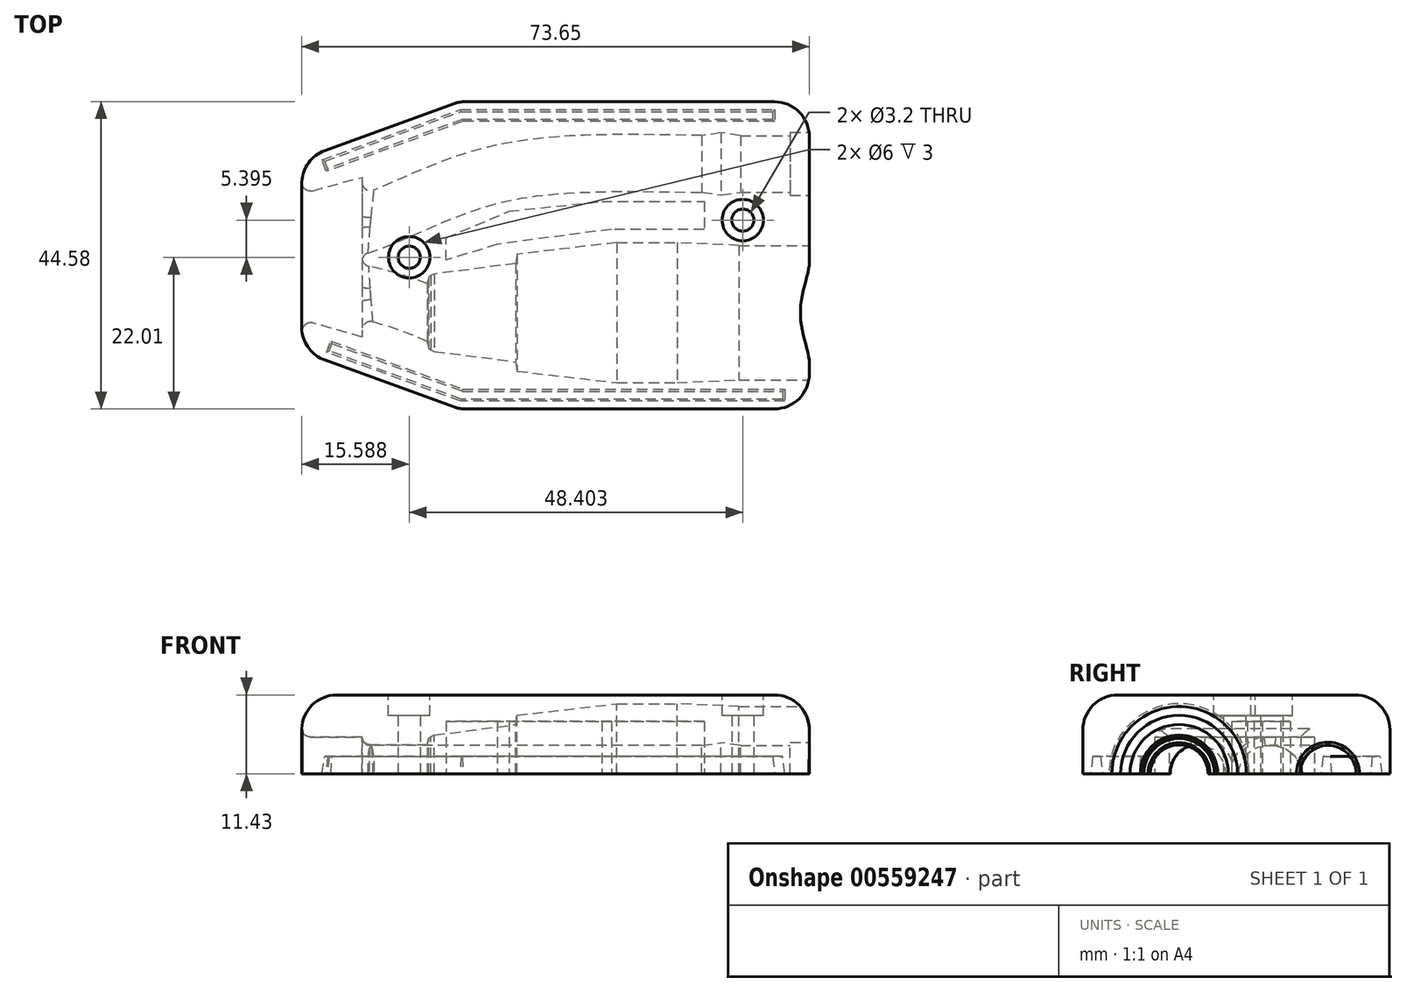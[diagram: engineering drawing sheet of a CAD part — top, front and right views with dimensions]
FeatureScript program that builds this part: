
annotation { "Feature Type Name" : "Feature", "Feature Type Description" : "" }
export const myFeature = defineFeature(function(context is Context, id is Id, definition is map)
    precondition{}
    {
        {
            var Q0;
            Q0=qCreatedBy(makeId("Top.planeOp"),FACE);
            var sketch = newSketch(context, id + "F0", { "sketchPlane" : qUnion([Q0])});
            skLineSegment(sketch, "E0", {"start": v(-29.16, 2.44) * mm, "end": v(45.25, 2.44) * mm});
            skLineSegment(sketch, "E1", {"start": v(45.25, 2.44) * mm, "end": v(45.25, -7.31) * mm});
            skLineSegment(sketch, "E2", {"start": v(45.25, -7.31) * mm, "end": v(33.01, -7.3) * mm});
            skLineSegment(sketch, "E3", {"start": v(33.01, -7.3) * mm, "end": v(31, -7.31) * mm});
            skLineSegment(sketch, "E4", {"start": v(31, -7.31) * mm, "end": v(16, -7.31) * mm});
            skLineSegment(sketch, "E5", {"start": v(16, -7.31) * mm, "end": v(7, -7.72) * mm});
            skLineSegment(sketch, "E6", {"start": v(7, -7.72) * mm, "end": v(-1.71, -7.72) * mm});
            skLineSegment(sketch, "E7", {"start": v(-1.71, -7.72) * mm, "end": v(-16.21, -6.04) * mm});
            skLineSegment(sketch, "E8", {"start": v(-16.21, -6.04) * mm, "end": v(-16.37, -4.7) * mm});
            skLineSegment(sketch, "E9", {"start": v(-16.37, -4.7) * mm, "end": v(-28.19, -3.17) * mm});
            skLineSegment(sketch, "E10", {"start": v(-28.19, -3.17) * mm, "end": v(-28.73, -2.96) * mm});
            skLineSegment(sketch, "E11", {"start": v(-28.73, -2.96) * mm, "end": v(-29.03, -2.68) * mm});
            skLineSegment(sketch, "E12", {"start": v(-29.03, -2.68) * mm, "end": v(-29.18, -2.06) * mm});
            skLineSegment(sketch, "E13", {"start": v(-29.18, -2.06) * mm, "end": v(-29.16, 2.44) * mm});
            skLineSegment(sketch, "E14.top", {"start": v(29.2, 18.83) * mm, "end": v(41.5, 18.83) * mm});
            skLineSegment(sketch, "E14.right", {"start": v(41.5, 24.03) * mm, "end": v(41.5, 18.83) * mm});
            skLineSegment(sketch, "E15", {"start": v(29.2, 19.46) * mm, "end": v(23.4, 19.46) * mm});
            skLineSegment(sketch, "E16", {"start": v(23.4, 19.46) * mm, "end": v(23.4, 24.03) * mm});
            skLineSegment(sketch, "E17", {"start": v(41.5, 24.03) * mm, "end": v(23.4, 24.03) * mm});
            skLineSegment(sketch, "E18", {"start": v(29.2, 18.83) * mm, "end": v(29.2, 19.46) * mm});
            skLineSegment(sketch, "E19.MirrorCS", {"start": v(-28.73, 7.85) * mm, "end": v(-29.03, 7.56) * mm});
            skLineSegment(sketch, "E20.MirrorCS", {"start": v(-29.03, 7.56) * mm, "end": v(-29.18, 6.94) * mm});
            skLineSegment(sketch, "E21.MirrorCS", {"start": v(33.01, 12.2) * mm, "end": v(31, 12.2) * mm});
            skLineSegment(sketch, "E22.MirrorCS", {"start": v(-28.19, 8.06) * mm, "end": v(-28.73, 7.85) * mm});
            skLineSegment(sketch, "E23.MirrorCS", {"start": v(-16.21, 10.93) * mm, "end": v(-16.37, 9.58) * mm});
            skLineSegment(sketch, "E24.MirrorCS", {"start": v(-16.37, 9.58) * mm, "end": v(-28.19, 8.06) * mm});
            skLineSegment(sketch, "E25.MirrorCS", {"start": v(7, 12.6) * mm, "end": v(-1.71, 12.6) * mm});
            skLineSegment(sketch, "E26.MirrorCS", {"start": v(45.25, 12.2) * mm, "end": v(33.01, 12.2) * mm});
            skLineSegment(sketch, "E27.MirrorCS", {"start": v(-1.71, 12.6) * mm, "end": v(-16.21, 10.93) * mm});
            skLineSegment(sketch, "E28.MirrorCS", {"start": v(16, 12.2) * mm, "end": v(7, 12.6) * mm});
            skLineSegment(sketch, "E29.MirrorCS", {"start": v(31, 12.2) * mm, "end": v(16, 12.2) * mm});
            skLineSegment(sketch, "E30.MirrorCS", {"start": v(45.25, 2.44) * mm, "end": v(45.25, 12.2) * mm});
            skLineSegment(sketch, "E31.MirrorCS", {"start": v(-29.18, 6.94) * mm, "end": v(-29.16, 2.44) * mm});
            skLineSegment(sketch, "E32", {"start": v(41.5, 20.03) * mm, "end": v(44.1, 20.03) * mm});
            skLineSegment(sketch, "E33", {"start": v(44.1, 20.03) * mm, "end": v(44.1, 24.03) * mm});
            skLineSegment(sketch, "E34", {"start": v(44.1, 24.03) * mm, "end": v(41.5, 24.03) * mm});
            skLineSegment(sketch, "E35", {"start": v(44.1, 20.03) * mm, "end": v(44.1, 19.46) * mm});
            skLineSegment(sketch, "E36", {"start": v(44.1, 19.46) * mm, "end": v(45.25, 19.46) * mm});
            skLineSegment(sketch, "E37", {"start": v(45.25, 19.46) * mm, "end": v(45.32, 24.03) * mm});
            skLineSegment(sketch, "E38", {"start": v(45.32, 24.03) * mm, "end": v(44.1, 24.03) * mm});
            skLineSegment(sketch, "E39", {"start": v(23.4, 24.03) * mm, "end": v(16.2, 24.03) * mm});
            skLineSegment(sketch, "E40", {"start": v(16.2, 24.03) * mm, "end": v(16.2, 19.93) * mm});
            skLineSegment(sketch, "E41", {"start": v(16.2, 19.93) * mm, "end": v(23.4, 19.93) * mm});
            skLineSegment(sketch, "E42", {"start": v(16.2, 19.93) * mm, "end": v(13.4, 19.53) * mm});
            skLineSegment(sketch, "E43", {"start": v(13.4, 19.53) * mm, "end": v(10.6, 19.93) * mm});
            skLineSegment(sketch, "E44", {"start": v(10.6, 19.93) * mm, "end": v(10.6, 24.03) * mm});
            skLineSegment(sketch, "E45", {"start": v(10.6, 24.03) * mm, "end": v(16.2, 24.03) * mm});
            skLineSegment(sketch, "E46.MirrorCS", {"start": v(44.1, 28.03) * mm, "end": v(44.1, 28.6) * mm});
            skLineSegment(sketch, "E47.MirrorCS", {"start": v(44.1, 28.6) * mm, "end": v(45.25, 28.6) * mm});
            skLineSegment(sketch, "E48.MirrorCS", {"start": v(29.2, 29.24) * mm, "end": v(29.2, 28.6) * mm});
            skLineSegment(sketch, "E49.MirrorCS", {"start": v(44.1, 28.03) * mm, "end": v(44.1, 24.03) * mm});
            skLineSegment(sketch, "E50.MirrorCS", {"start": v(16.2, 24.03) * mm, "end": v(16.2, 28.13) * mm});
            skLineSegment(sketch, "E51.MirrorCS", {"start": v(23.4, 28.6) * mm, "end": v(23.4, 24.03) * mm});
            skLineSegment(sketch, "E52.MirrorCS", {"start": v(10.6, 28.13) * mm, "end": v(10.6, 24.03) * mm});
            skLineSegment(sketch, "E53.MirrorCS", {"start": v(29.2, 28.6) * mm, "end": v(23.4, 28.6) * mm});
            skLineSegment(sketch, "E54.MirrorCS", {"start": v(41.5, 24.03) * mm, "end": v(41.5, 29.24) * mm});
            skLineSegment(sketch, "E55.MirrorCS", {"start": v(29.2, 29.24) * mm, "end": v(41.5, 29.24) * mm});
            skLineSegment(sketch, "E56.MirrorCS", {"start": v(45.25, 28.6) * mm, "end": v(45.32, 24.03) * mm});
            skLineSegment(sketch, "E57.MirrorCS", {"start": v(13.4, 28.53) * mm, "end": v(10.6, 28.13) * mm});
            skLineSegment(sketch, "E58.MirrorCS", {"start": v(41.5, 28.03) * mm, "end": v(44.1, 28.03) * mm});
            skLineSegment(sketch, "E59.MirrorCS", {"start": v(16.2, 28.13) * mm, "end": v(13.4, 28.53) * mm});
            skLineSegment(sketch, "E60.MirrorCS", {"start": v(16.2, 28.13) * mm, "end": v(23.4, 28.13) * mm});
            skSolve(sketch);
        }
        {
            var Q0;
            Q0=qCreatedBy(makeId("Top.planeOp"),FACE);
            var sketch = newSketch(context, id + "F1", { "sketchPlane" : qUnion([Q0])});
            skLineSegment(sketch, "E61.0", {"start": v(45.25, 2.44) * mm, "end": v(45.25, -7.31) * mm});
            skLineSegment(sketch, "E62", {"start": v(26.2, 33.05) * mm, "end": v(26.2, -11.53) * mm});
            skLineSegment(sketch, "E63", {"start": v(26.2, -11.53) * mm, "end": v(-24.6, -11.53) * mm});
            skLineSegment(sketch, "E64", {"start": v(-24.6, -11.53) * mm, "end": v(-47.46, -3.2) * mm});
            skLineSegment(sketch, "E65", {"start": v(-47.46, -3.2) * mm, "end": v(-47.46, 24.73) * mm});
            skLineSegment(sketch, "E66", {"start": v(-47.46, 24.73) * mm, "end": v(-24.6, 33.05) * mm});
            skLineSegment(sketch, "E67", {"start": v(-24.6, 33.05) * mm, "end": v(26.2, 33.05) * mm});
            skLineSegment(sketch, "E68.0", {"start": v(29.2, 29.24) * mm, "end": v(41.5, 29.24) * mm});
            skSolve(sketch);
        }
        {
            var Q0;
            Q0=qSketchRegion(id+"F1",true);
            extrude(context, id + "F2", {"entities" : qUnion([Q0]), "oppositeDirection" : true, "depth" : 0 * mm, "offsetDistance" : 25.4 * mm, "hasSecondDirection" : true, "secondDirectionOppositeDirection" : false, "secondDirectionDepth" : 11.43 * mm});
        }
        {
            var Q0;
            Q0=makeQuery(id+"F0.imprint","IMPRINT",FACE,{"disambiguationData":[TD([[makeQuery(id+"F0.imprint","IMPRINT",EDGE,{"derivedFrom":sQuery(id+"F0.wireOp",EDGE,"E0")}),-1.0]])]});
            var Q1;
            Q1=sQuery(id+"F0.wireOp",EDGE,"E0");
            revolve(context, id + "F3", {"operationType" : NewBodyOperationType.REMOVE, "entities" : qUnion([Q0]), "axis" : qUnion([Q1]), "revolveType" : RevolveType.FULL, "oppositeDirection" : true});
        }
        {
            var Q0;
            Q0=makeQuery(id+"F0.imprint","IMPRINT",FACE,{"disambiguationData":[TD([[makeQuery(id+"F0.imprint","IMPRINT",EDGE,{"derivedFrom":sQuery(id+"F0.wireOp",EDGE,"E14.top")}),1.0]])]});
            var Q1;
            Q1=makeQuery(id+"F0.imprint","IMPRINT",FACE,{"disambiguationData":[TD([[makeQuery(id+"F0.imprint","IMPRINT",EDGE,{"derivedFrom":sQuery(id+"F0.wireOp",EDGE,"E40")}),1.0]])]});
            var Q2;
            Q2=makeQuery(id+"F0.imprint","IMPRINT",FACE,{"disambiguationData":[TD([[makeQuery(id+"F0.imprint","IMPRINT",EDGE,{"derivedFrom":sQuery(id+"F0.wireOp",EDGE,"E40")}),-1.0]])]});
            var Q3;
            Q3=sQuery(id+"F0.wireOp",EDGE,"E17");
            revolve(context, id + "F4", {"operationType" : NewBodyOperationType.REMOVE, "entities" : qUnion([Q0, Q1, Q2]), "axis" : qUnion([Q3]), "revolveType" : RevolveType.FULL});
        }
        {
            var Q0;
            Q0=makeQuery(id+"F2.opExtrude","CAP_FACE",FACE,{"disambiguationData":[OSD([sQuery(id+"F1.wireOp",EDGE,"FN9DgEXL-DUnT-EqR8-ggIH-wTex11pTKOJ6"),sQuery(id+"F1.wireOp",EDGE,"Mmaicck8-LA38-ALDy-QV3c-pMFCgAv4KP83"),sQuery(id+"F1.wireOp",EDGE,"E62"),sQuery(id+"F1.wireOp",EDGE,"E63"),sQuery(id+"F1.wireOp",EDGE,"E64"),sQuery(id+"F1.wireOp",EDGE,"E65"),sQuery(id+"F1.wireOp",EDGE,"E66"),sQuery(id+"F1.wireOp",EDGE,"E67")])],"isStart":true});
            var sketch = newSketch(context, id + "F5", { "sketchPlane" : qUnion([Q0])});
            skLineSegment(sketch, "E69.0", {"start": v(-29.16, 2.44) * mm, "end": v(45.25, 2.44) * mm});
            skFitSpline(sketch, "E70", {"points": [v(-29.16, 2.44) * mm, v(-47.46, 6.7) * mm, v(-83.77, 9.93) * mm], "startDerivative": vector(-48.46, 20.5) * mm, "endDerivative": vector(-77.25, 2.74) * mm});
            skSolve(sketch);
        }
        {
            var Q0;
            Q0=sQuery(id+"F5.wireOp",VERTEX,"E70.0.internal");
            var Q1;
            Q1=sQuery(id+"F5.wireOp",EDGE,"E69.0");
            cPlane(context, id + "F6", {"entities" : qUnion([Q0, Q1]), "cplaneType" : CPlaneType.LINE_POINT, "offset" : 25.4 * mm, "width" : 152.4 * mm, "height" : 152.4 * mm});
        }
        {
            var Q0;
            Q0=qCreatedBy(id+"F6.planeOp",FACE);
            var sketch = newSketch(context, id + "F7", { "sketchPlane" : qUnion([Q0])});
            skCircle(sketch, "E71", {"center": v(2.44, 0) * mm, "radius": 4.2 * mm});
            skSolve(sketch);
        }
        {
            var Q0;
            Q0=qSketchRegion(id+"F7",true);
            var Q1;
            Q1=sQuery(id+"F5.wireOp",EDGE,"E70");
            sweep(context, id + "F8", {"operationType" : NewBodyOperationType.REMOVE, "profiles" : qUnion([Q0]), "path" : qUnion([Q1])});
        }
        {
            var Q0;
            Q0=sQuery(id+"F0.wireOp",VERTEX,"E45.start");
            var Q1;
            Q1=sQuery(id+"F0.wireOp",EDGE,"E45");
            cPlane(context, id + "F9", {"entities" : qUnion([Q0, Q1]), "cplaneType" : CPlaneType.LINE_POINT, "offset" : 25.4 * mm, "width" : 152.4 * mm, "height" : 152.4 * mm});
        }
        {
            var Q0;
            {var subQ0=sQuery(id+"F1.wireOp",EDGE,"E62");var subQ1=sQuery(id+"F1.wireOp",EDGE,"E65");var subQ2=sQuery(id+"F1.wireOp",EDGE,"E66");var subQ3=sQuery(id+"F1.wireOp",EDGE,"E67");Q0=makeQuery(id+"F8.boolean.opBoolean","SPLIT",FACE,{"disambiguationData":[TD([makeQuery(id+"F2.opExtrude","SWEPT_FACE",FACE,{"disambiguationData":[OSD([subQ2])]})])],"derivedFrom":makeQuery(id+"F2.opExtrude","CAP_FACE",FACE,{"disambiguationData":[OSD([subQ0,sQuery(id+"F1.wireOp",EDGE,"E63"),sQuery(id+"F1.wireOp",EDGE,"E64"),subQ1,subQ2,subQ3])],"isStart":true})});}
            var sketch = newSketch(context, id + "F10", { "sketchPlane" : qUnion([Q0])});
            skLineSegment(sketch, "E72.0", {"start": v(10.6, 24.03) * mm, "end": v(16.2, 24.03) * mm});
            skFitSpline(sketch, "E73", {"points": [v(10.6, 24.03) * mm, v(-17.54, 22.88) * mm, v(-35.92, 16.19) * mm, v(-61.27, 13.83) * mm], "startDerivative": vector(-66.57, 0.28) * mm, "endDerivative": vector(-121.3, 10.88) * mm});
            skSolve(sketch);
        }
        {
            var Q0;
            Q0=qCreatedBy(id+"F9.planeOp",FACE);
            var sketch = newSketch(context, id + "F11", { "sketchPlane" : qUnion([Q0])});
            skCircle(sketch, "E74", {"center": v(24.03, 0) * mm, "radius": 4.12 * mm});
            skSolve(sketch);
        }
        {
            var Q0;
            Q0=qSketchRegion(id+"F11",true);
            var Q1;
            Q1=sQuery(id+"F10.wireOp",EDGE,"E73");
            sweep(context, id + "F12", {"operationType" : NewBodyOperationType.REMOVE, "profiles" : qUnion([Q0]), "path" : qUnion([Q1])});
        }
        {
            var Q0;
            Q0=qCreatedBy(makeId("Top.planeOp"),FACE);
            var sketch = newSketch(context, id + "F13", { "sketchPlane" : qUnion([Q0])});
            skLineSegment(sketch, "E75.0", {"start": v(-24.4, 31.92) * mm, "end": v(21.2, 31.92) * mm});
            skLineSegment(sketch, "E75.1", {"start": v(-44.5, 24.6) * mm, "end": v(-24.4, 31.92) * mm});
            skPoint(sketch, "E76", {"position": v(21.2, 31.92) * mm});
            skPoint(sketch, "E77", {"position": v(-44.5, 24.6) * mm});
            skLineSegment(sketch, "E78.0", {"start": v(-24.09, 30.17) * mm, "end": v(21.2, 30.17) * mm});
            skLineSegment(sketch, "E78.1", {"start": v(-43.91, 22.96) * mm, "end": v(-24.09, 30.17) * mm});
            skLineSegment(sketch, "E79", {"start": v(21.2, 30.17) * mm, "end": v(21.2, 31.92) * mm});
            skLineSegment(sketch, "E80", {"start": v(-44.5, 24.6) * mm, "end": v(-43.91, 22.96) * mm});
            skLineSegment(sketch, "E81.0", {"start": v(-24.4, -10.4) * mm, "end": v(-43.83, -3.33) * mm});
            skLineSegment(sketch, "E81.1", {"start": v(22.64, -10.4) * mm, "end": v(-24.4, -10.4) * mm});
            skPoint(sketch, "E82", {"position": v(22.64, -10.4) * mm});
            skPoint(sketch, "E83", {"position": v(-43.83, -3.33) * mm});
            skLineSegment(sketch, "E84.0", {"start": v(-24.09, -8.65) * mm, "end": v(-43.24, -1.68) * mm});
            skLineSegment(sketch, "E84.1", {"start": v(22.64, -8.65) * mm, "end": v(-24.09, -8.65) * mm});
            skLineSegment(sketch, "E85", {"start": v(22.64, -10.4) * mm, "end": v(22.64, -8.65) * mm});
            skLineSegment(sketch, "E86", {"start": v(-43.83, -3.33) * mm, "end": v(-43.24, -1.68) * mm});
            skSolve(sketch);
        }
        {
            var Q0;
            Q0=qCreatedBy(makeId("Top.planeOp"),FACE);
            var sketch = newSketch(context, id + "F14", { "sketchPlane" : qUnion([Q0])});
            skLineSegment(sketch, "E87", {"start": v(-48.77, 19.31) * mm, "end": v(-38.71, 22.1) * mm});
            skLineSegment(sketch, "E88", {"start": v(-38.71, 22.1) * mm, "end": v(-38.71, -1.1) * mm});
            skLineSegment(sketch, "E89", {"start": v(-38.71, -1.1) * mm, "end": v(-48.92, 1.83) * mm});
            skLineSegment(sketch, "E90", {"start": v(-48.92, 1.83) * mm, "end": v(-48.77, 19.31) * mm});
            skSolve(sketch);
        }
        {
            var Q0;
            Q0=qCreatedBy(makeId("Top.planeOp"),FACE);
            var sketch = newSketch(context, id + "F15", { "sketchPlane" : qUnion([Q0])});
            skCircle(sketch, "E91", {"center": v(-31.86, 10.48) * mm, "radius": 1.6 * mm});
            skCircle(sketch, "E92", {"center": v(16.54, 15.88) * mm, "radius": 1.6 * mm});
            skSolve(sketch);
        }
        {
            var Q0;
            Q0 = qSketchRegion(id + "F13", true);
            extrude(context, id + "F16", {"entities" : qUnion([Q0]), "operationType" : NewBodyOperationType.REMOVE, "depth" : 2.5 * mm, "offsetDistance" : 25.4 * mm, "hasDraft" : true, "draftAngle" : 7 * degree, "draftPullDirection" : true});
        }
        {
            var Q0;
            Q0 = qSketchRegion(id + "F15", true);
            extrude(context, id + "F17", {"entities" : qUnion([Q0]), "operationType" : NewBodyOperationType.REMOVE, "depth" : 25.4 * mm, "offsetDistance" : 25.4 * mm});
        }
        {
            var Q0;
            Q0 = qSketchRegion(id + "F14", true);
            extrude(context, id + "F18", {"entities" : qUnion([Q0]), "operationType" : NewBodyOperationType.REMOVE, "depth" : 5.33 * mm, "offsetDistance" : 25.4 * mm});
        }
        {
            var Q0;
            Q0=makeQuery(id+"F2.opExtrude","CAP_FACE",FACE,{"disambiguationData":[OSD([sQuery(id+"F1.wireOp",EDGE,"E62"),sQuery(id+"F1.wireOp",EDGE,"E63"),sQuery(id+"F1.wireOp",EDGE,"E64"),sQuery(id+"F1.wireOp",EDGE,"E65"),sQuery(id+"F1.wireOp",EDGE,"E66"),sQuery(id+"F1.wireOp",EDGE,"E67")])],"isStart":true});
            var sketch = newSketch(context, id + "F19", { "sketchPlane" : qUnion([Q0])});
            skCircle(sketch, "E93.0", {"center": v(-31.86, 10.48) * mm, "radius": 1.6 * mm});
            skCircle(sketch, "E94.0", {"center": v(16.54, 15.88) * mm, "radius": 1.6 * mm});
            skCircle(sketch, "E95", {"center": v(-31.86, 10.48) * mm, "radius": 3 * mm});
            skCircle(sketch, "E96", {"center": v(16.54, 15.88) * mm, "radius": 3 * mm});
            skSolve(sketch);
        }
        {
            var Q0;
            Q0 = qSketchRegion(id + "F19", true);
            extrude(context, id + "F20", {"entities" : qUnion([Q0]), "operationType" : NewBodyOperationType.REMOVE, "oppositeDirection" : true, "depth" : 3 * mm, "offsetDistance" : 25.4 * mm});
        }
        {
            var Q0;
            {var subQ4=sQuery(id+"F1.wireOp",EDGE,"E62");var subQ8=makeQuery(id+"F3.boolean.opBoolean","COPY",FACE,{"derivedFrom":makeQuery(id+"F3.opRevolve","SWEPT_FACE",FACE,{"disambiguationData":[OSD([sQuery(id+"F0.wireOp",EDGE,"E4")])]})});var subQ19=sQuery(id+"F1.wireOp",EDGE,"E65");var subQ20=sQuery(id+"F1.wireOp",EDGE,"E66");var subQ21=sQuery(id+"F1.wireOp",EDGE,"E67");Q0=makeQuery(id+"F12.boolean.opBoolean","SPLIT",FACE,{"disambiguationData":[TD([subQ8])],"derivedFrom":makeQuery(id+"F8.boolean.opBoolean","SPLIT",FACE,{"disambiguationData":[TD([makeQuery(id+"F2.opExtrude","SWEPT_FACE",FACE,{"disambiguationData":[OSD([subQ20])]})])],"derivedFrom":makeQuery(id+"F2.opExtrude","CAP_FACE",FACE,{"disambiguationData":[OSD([subQ4,sQuery(id+"F1.wireOp",EDGE,"E63"),sQuery(id+"F1.wireOp",EDGE,"E64"),subQ19,subQ20,subQ21])],"isStart":false})})});}
            var sketch = newSketch(context, id + "F21", { "sketchPlane" : qUnion([Q0])});
            skLineSegment(sketch, "E97", {"start": v(-26.5, -13.3) * mm, "end": v(-17.37, -17.17) * mm});
            skLineSegment(sketch, "E98", {"start": v(-17.37, -17.17) * mm, "end": v(-3.92, -18.56) * mm});
            skLineSegment(sketch, "E99", {"start": v(-3.92, -18.56) * mm, "end": v(10.93, -18.56) * mm});
            skLineSegment(sketch, "E100", {"start": v(10.93, -18.56) * mm, "end": v(10.93, -14.54) * mm});
            skLineSegment(sketch, "E101", {"start": v(10.93, -14.54) * mm, "end": v(-2.52, -14.54) * mm});
            skLineSegment(sketch, "E102", {"start": v(-2.52, -14.54) * mm, "end": v(-19.07, -12.37) * mm});
            skLineSegment(sketch, "E103", {"start": v(-19.07, -12.37) * mm, "end": v(-26.5, -10.05) * mm});
            skLineSegment(sketch, "E104", {"start": v(-26.5, -10.05) * mm, "end": v(-26.5, -13.3) * mm});
            skSolve(sketch);
        }
        {
            var Q0;
            Q0 = qSketchRegion(id + "F21", true);
            extrude(context, id + "F22", {"entities" : qUnion([Q0]), "operationType" : NewBodyOperationType.REMOVE, "oppositeDirection" : true, "depth" : 7.62 * mm, "offsetDistance" : 25.4 * mm});
        }
        {
            var Q0;
            Q0=makeQuery(id+"F2.opExtrude","CAP_EDGE",EDGE,{"disambiguationData":[OSD([sQuery(id+"F1.wireOp",EDGE,"E65")])],"isStart":true});
            var Q1;
            Q1=makeQuery(id+"F2.opExtrude","SWEPT_EDGE",EDGE,{"disambiguationData":[OSD([sQuery(id+"F1.wireOp",EDGE,"E64"),sQuery(id+"F1.wireOp",EDGE,"E65")])]});
            var Q2;
            Q2=makeQuery(id+"F2.opExtrude","CAP_EDGE",EDGE,{"disambiguationData":[OSD([sQuery(id+"F1.wireOp",EDGE,"E64")])],"isStart":true});
            var Q3;
            Q3=makeQuery(id+"F2.opExtrude","SWEPT_EDGE",EDGE,{"disambiguationData":[OSD([sQuery(id+"F1.wireOp",EDGE,"E63"),sQuery(id+"F1.wireOp",EDGE,"E64")])]});
            var Q4;
            Q4=makeQuery(id+"F2.opExtrude","CAP_EDGE",EDGE,{"disambiguationData":[OSD([sQuery(id+"F1.wireOp",EDGE,"E63")])],"isStart":true});
            var Q5;
            Q5=makeQuery(id+"F2.opExtrude","SWEPT_EDGE",EDGE,{"disambiguationData":[OSD([sQuery(id+"F1.wireOp",EDGE,"E62"),sQuery(id+"F1.wireOp",EDGE,"E63")])]});
            var Q6;
            Q6=makeQuery(id+"F2.opExtrude","CAP_EDGE",EDGE,{"disambiguationData":[OSD([sQuery(id+"F1.wireOp",EDGE,"E62")])],"isStart":true});
            var Q7;
            Q7=makeQuery(id+"F2.opExtrude","SWEPT_EDGE",EDGE,{"disambiguationData":[OSD([sQuery(id+"F1.wireOp",EDGE,"E62"),sQuery(id+"F1.wireOp",EDGE,"E67")])]});
            var Q8;
            Q8=makeQuery(id+"F2.opExtrude","CAP_EDGE",EDGE,{"disambiguationData":[OSD([sQuery(id+"F1.wireOp",EDGE,"E67")])],"isStart":true});
            var Q9;
            Q9=makeQuery(id+"F2.opExtrude","SWEPT_EDGE",EDGE,{"disambiguationData":[OSD([sQuery(id+"F1.wireOp",EDGE,"E66"),sQuery(id+"F1.wireOp",EDGE,"E67")])]});
            var Q10;
            Q10=makeQuery(id+"F2.opExtrude","CAP_EDGE",EDGE,{"disambiguationData":[OSD([sQuery(id+"F1.wireOp",EDGE,"E66")])],"isStart":true});
            var Q11;
            Q11=makeQuery(id+"F2.opExtrude","SWEPT_EDGE",EDGE,{"disambiguationData":[OSD([sQuery(id+"F1.wireOp",EDGE,"E65"),sQuery(id+"F1.wireOp",EDGE,"E66")])]});
            fillet(context, id + "F23", {"entities" : qUnion([Q0, Q1, Q2, Q3, Q4, Q5, Q6, Q7, Q8, Q9, Q10, Q11]), "radius" : 5.08 * mm, "tangentPropagation" : true, "allowEdgeOverflow" : false});
        }
        {
            var Q0;
            Q0=makeQuery(id+"F18.boolean.opBoolean","INTERSECT",EDGE,{"derivedFrom":[makeQuery(id+"F8.boolean.opBoolean","COPY",FACE,{"derivedFrom":makeQuery(id+"F8.opSweep","SWEPT_FACE",FACE,{"disambiguationData":[OSD([sQuery(id+"F5.wireOp",EDGE,"E70"),sQuery(id+"F7.wireOp",EDGE,"E71")])]})}),makeQuery(id+"F18.opExtrude","SWEPT_FACE",FACE,{"disambiguationData":[OSD([sQuery(id+"F14.wireOp",EDGE,"E88")])]})]});
            var Q1;
            Q1=makeQuery(id+"F18.boolean.opBoolean","INTERSECT",EDGE,{"derivedFrom":[makeQuery(id+"F12.boolean.opBoolean","COPY",FACE,{"derivedFrom":makeQuery(id+"F12.opSweep","SWEPT_FACE",FACE,{"disambiguationData":[OSD([sQuery(id+"F10.wireOp",EDGE,"E73"),sQuery(id+"F11.wireOp",EDGE,"E74")])]})}),makeQuery(id+"F18.opExtrude","SWEPT_FACE",FACE,{"disambiguationData":[OSD([sQuery(id+"F14.wireOp",EDGE,"E88")])]})]});
            var Q2;
            Q2=makeQuery(id+"F18.boolean.opBoolean","INTERSECT",EDGE,{"derivedFrom":[makeQuery(id+"F2.opExtrude","SWEPT_FACE",FACE,{"disambiguationData":[OSD([sQuery(id+"F1.wireOp",EDGE,"E65")])]}),makeQuery(id+"F18.opExtrude","CAP_FACE",FACE,{"disambiguationData":[OSD([sQuery(id+"F14.wireOp",EDGE,"E87"),sQuery(id+"F14.wireOp",EDGE,"E88"),sQuery(id+"F14.wireOp",EDGE,"E89"),sQuery(id+"F14.wireOp",EDGE,"E90")])],"isStart":false})]});
            fillet(context, id + "F24", {"entities" : qUnion([Q0, Q1, Q2]), "radius" : 1.27 * mm, "tangentPropagation" : true, "allowEdgeOverflow" : false});
        }
        {
            var Q0;
            Q0=makeQuery(id+"F18.boolean.opBoolean","INTERSECT",EDGE,{"derivedFrom":[makeQuery(id+"F2.opExtrude","SWEPT_FACE",FACE,{"disambiguationData":[OSD([sQuery(id+"F1.wireOp",EDGE,"E65")])]}),makeQuery(id+"F18.opExtrude","SWEPT_FACE",FACE,{"disambiguationData":[OSD([sQuery(id+"F14.wireOp",EDGE,"E87")])]})]});
            var Q1;
            Q1=makeQuery(id+"F18.boolean.opBoolean","INTERSECT",EDGE,{"derivedFrom":[makeQuery(id+"F2.opExtrude","SWEPT_FACE",FACE,{"disambiguationData":[OSD([sQuery(id+"F1.wireOp",EDGE,"E65")])]}),makeQuery(id+"F18.opExtrude","SWEPT_FACE",FACE,{"disambiguationData":[OSD([sQuery(id+"F14.wireOp",EDGE,"E89")])]})]});
            fillet(context, id + "F25", {"entities" : qUnion([Q0, Q1]), "radius" : 1.27 * mm, "tangentPropagation" : true, "allowEdgeOverflow" : false});
        }
    });
